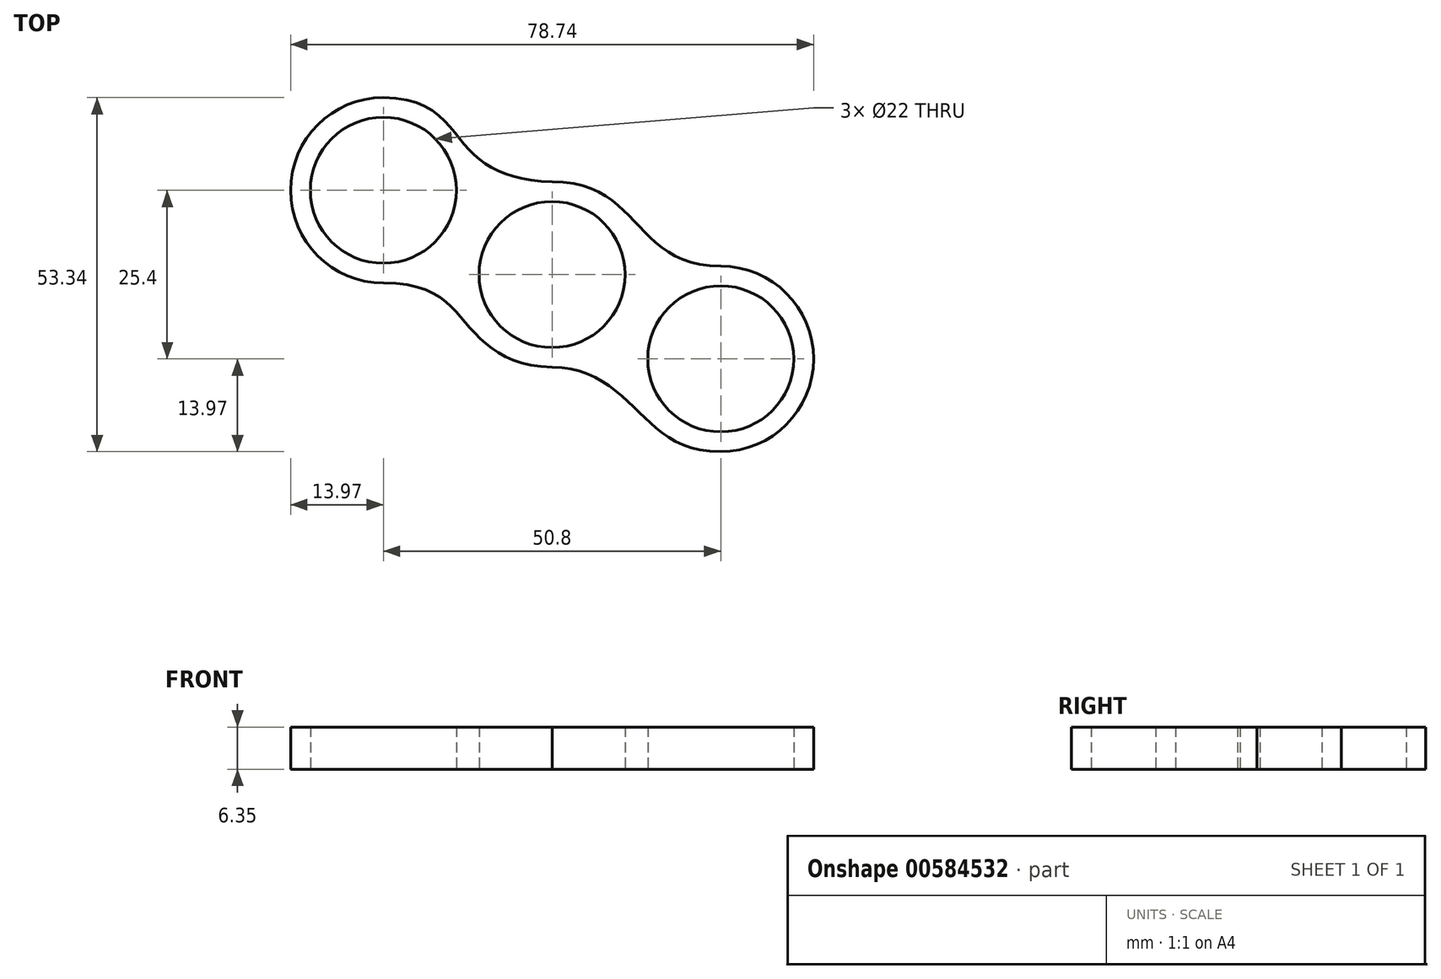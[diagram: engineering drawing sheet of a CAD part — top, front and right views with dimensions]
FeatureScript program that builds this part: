
annotation { "Feature Type Name" : "Feature", "Feature Type Description" : "" }
export const myFeature = defineFeature(function(context is Context, id is Id, definition is map)
    precondition{}
    {
        {
            var Q0;
            Q0=qCreatedBy(makeId("Top.planeOp"),FACE);
            var sketch = newSketch(context, id + "F0", { "sketchPlane" : qUnion([Q0])});
            skCircle(sketch, "E0", {"center": v(0, 0) * mm, "radius": 11 * mm});
            skLineSegment(sketch, "E1", {"start": v(0, -13.97) * mm, "end": v(0, -13.97) * mm});
            skCircle(sketch, "E2", {"center": v(25.4, -12.7) * mm, "radius": 11 * mm});
            skArc(sketch, "E3", {"start": v(25.4, -26.67) * mm, "mid": v(39.37, -12.7) * mm, "end": v(25.4, 1.27) * mm});
            skCircle(sketch, "E4", {"center": v(-25.4, 12.7) * mm, "radius": 11 * mm});
            skArc(sketch, "E5", {"start": v(-25.4, 26.67) * mm, "mid": v(-39.37, 12.7) * mm, "end": v(-25.4, -1.27) * mm});
            skFitSpline(sketch, "E6", {"points": [v(-25.4, 26.67) * mm, v(-12.7, 19.05) * mm, v(0, 13.97) * mm], "startDerivative": vector(45.99, 0) * mm, "endDerivative": vector(39.43, -1.54) * mm});
            skFitSpline(sketch, "E7", {"points": [v(-25.4, -1.27) * mm, v(-12.7, -7.62) * mm, v(0, -13.97) * mm], "startDerivative": vector(46.9, 0) * mm, "endDerivative": vector(40.07, -1.02) * mm});
            skFitSpline(sketch, "E8", {"points": [v(0, 13.97) * mm, v(12.75, 7.62) * mm, v(25.4, 1.27) * mm], "startDerivative": vector(41.05, 0) * mm, "endDerivative": vector(39.4, 0) * mm});
            skFitSpline(sketch, "E9", {"points": [v(0, -13.97) * mm, v(12.7, -20.32) * mm, v(25.4, -26.67) * mm], "startDerivative": vector(34.67, 0) * mm, "endDerivative": vector(39.82, 0) * mm});
            skSolve(sketch);
        }
        {
            var Q0;
            Q0 = qSketchRegion(id + "F0", true);
            extrude(context, id + "F1", {"entities" : qUnion([Q0]), "depth" : 6.35 * mm, "offsetDistance" : 25.4 * mm});
        }
    });
